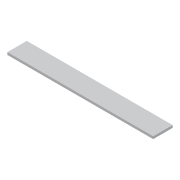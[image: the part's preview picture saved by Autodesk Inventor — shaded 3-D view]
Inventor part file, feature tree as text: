
AUTODESK INVENTOR PART (.ipt)
format: ipt  version: 2016 (Build 200138000, 138)  size: 66,048 bytes
history: native  units: mm
features: extrude x1, sketch x1
ambient origin geometry x8: Origin, YZ Plane, XZ Plane, XY Plane, X Axis, Y Axis, Z Axis, Center Point
bodies: Volumenkörper1 (feature_tree)
feature tree (2):
  extrude  "Extrusion1"  Depth=80.0mm
  sketch  "Skizze1"  dims[d0=600.0mm d1=80.0mm d2=10.0mm d3=0.0mm]
